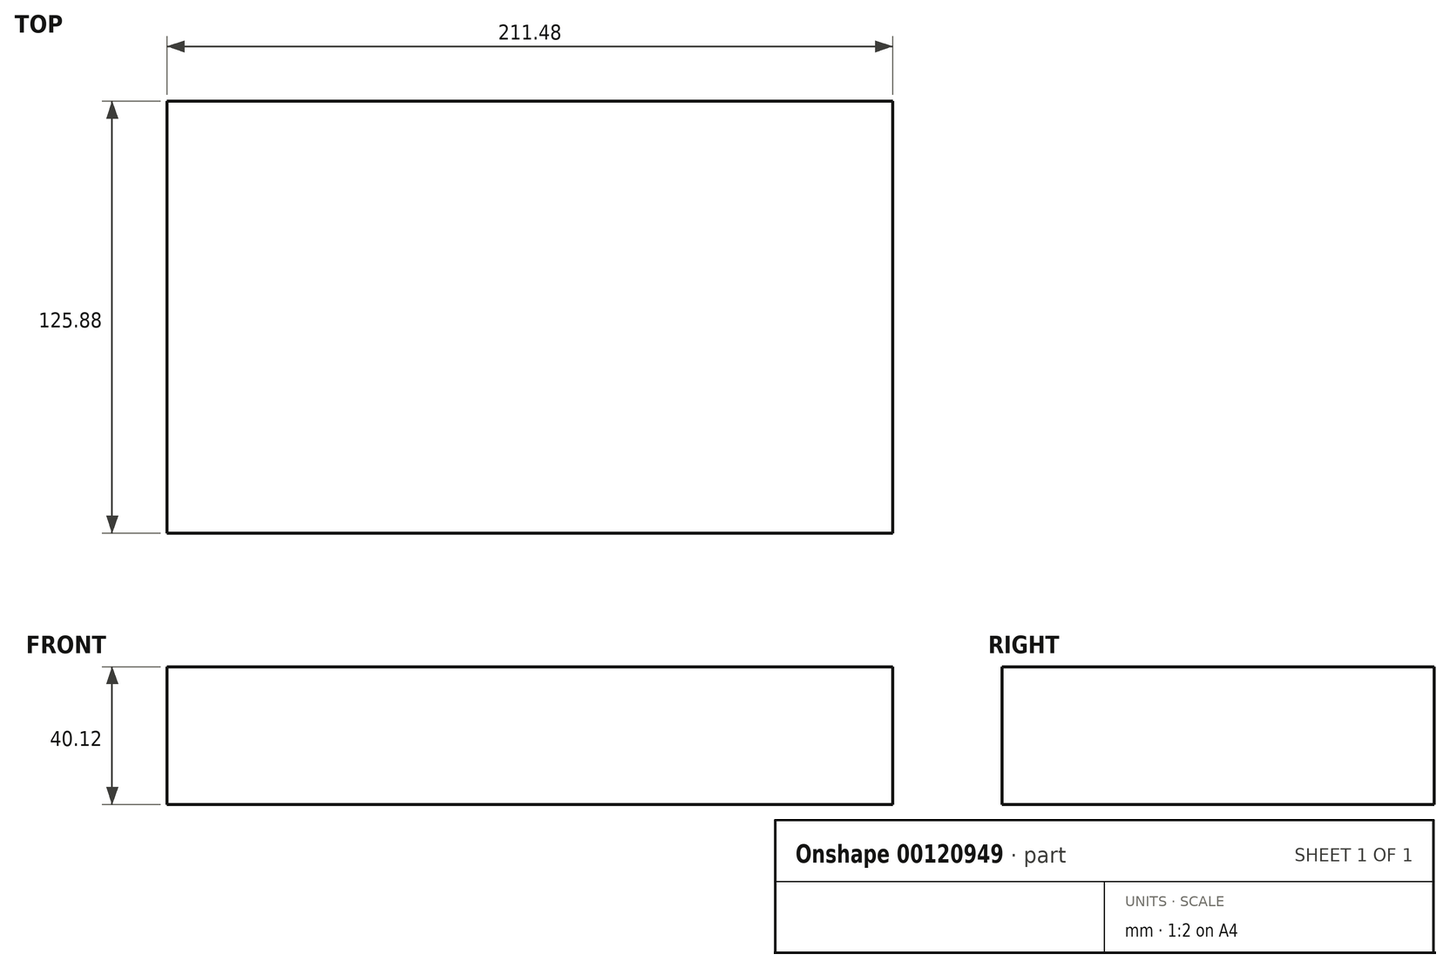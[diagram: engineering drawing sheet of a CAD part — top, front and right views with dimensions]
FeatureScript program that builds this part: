
annotation { "Feature Type Name" : "Feature", "Feature Type Description" : "" }
export const myFeature = defineFeature(function(context is Context, id is Id, definition is map)
    precondition{}
    {
        {
            var Q0;
            Q0=qCreatedBy(makeId("Top.planeOp"),FACE);
            var sketch = newSketch(context, id + "F0", { "sketchPlane" : qUnion([Q0])});
            skLineSegment(sketch, "E0.bottom", {"start": v(-96.13, 62.85) * mm, "end": v(115.35, 62.85) * mm});
            skLineSegment(sketch, "E0.top", {"start": v(-96.13, -63.03) * mm, "end": v(115.35, -63.03) * mm});
            skLineSegment(sketch, "E0.left", {"start": v(-96.13, 62.85) * mm, "end": v(-96.13, -63.03) * mm});
            skLineSegment(sketch, "E0.right", {"start": v(115.35, 62.85) * mm, "end": v(115.35, -63.03) * mm});
            skSolve(sketch);
        }
        {
            var Q0;
            Q0=qCreatedBy(makeId("Top.planeOp"),FACE);
            var sketch = newSketch(context, id + "F1", { "sketchPlane" : qUnion([Q0])});
            skLineSegment(sketch, "E1", {"start": v(-4.14, 45.72) * mm, "end": v(0, 45.72) * mm});
            skLineSegment(sketch, "E2", {"start": v(0, 45.72) * mm, "end": v(0, 38.86) * mm});
            skLineSegment(sketch, "E3", {"start": v(0, 38.86) * mm, "end": v(66.04, 38.86) * mm});
            skLineSegment(sketch, "E4", {"start": v(66.04, 38.86) * mm, "end": v(66.04, -38.86) * mm});
            skLineSegment(sketch, "E5", {"start": v(66.04, -38.86) * mm, "end": v(0, -38.86) * mm});
            skLineSegment(sketch, "E6", {"start": v(0, -38.86) * mm, "end": v(0, -45.72) * mm});
            skLineSegment(sketch, "E7", {"start": v(0, -45.72) * mm, "end": v(-4.14, -45.72) * mm});
            skLineSegment(sketch, "E8", {"start": v(-4.14, -45.72) * mm, "end": v(-4.14, 45.72) * mm});
            skSolve(sketch);
        }
        {
            var Q0;
            Q0=qCreatedBy(makeId("Top.planeOp"),FACE);
            var sketch = newSketch(context, id + "F2", { "sketchPlane" : qUnion([Q0])});
            skLineSegment(sketch, "E9", {"start": v(-4.14, -45.72) * mm, "end": v(-21.09, -45.72) * mm});
            skLineSegment(sketch, "E10", {"start": v(-21.09, -55.88) * mm, "end": v(-21.09, -45.72) * mm});
            skLineSegment(sketch, "E11", {"start": v(-21.09, -55.88) * mm, "end": v(-46.49, -55.88) * mm});
            skLineSegment(sketch, "E12", {"start": v(-46.49, -45.72) * mm, "end": v(-46.49, -55.88) * mm});
            skLineSegment(sketch, "E13", {"start": v(-46.49, -45.72) * mm, "end": v(-66.04, -45.72) * mm});
            skLineSegment(sketch, "E14", {"start": v(-66.04, 45.72) * mm, "end": v(-66.04, -45.72) * mm});
            skLineSegment(sketch, "E15", {"start": v(-66.04, 45.72) * mm, "end": v(-46.48, 45.72) * mm});
            skLineSegment(sketch, "E16", {"start": v(-46.48, 55.88) * mm, "end": v(-46.48, 45.72) * mm});
            skLineSegment(sketch, "E17", {"start": v(-46.48, 55.88) * mm, "end": v(-21.08, 55.88) * mm});
            skLineSegment(sketch, "E18", {"start": v(-21.08, 45.72) * mm, "end": v(-21.08, 55.88) * mm});
            skLineSegment(sketch, "E19", {"start": v(-21.08, 45.72) * mm, "end": v(-4.14, 45.72) * mm});
            skLineSegment(sketch, "E20", {"start": v(-4.14, -45.72) * mm, "end": v(-4.14, 45.72) * mm});
            skSolve(sketch);
        }
        {
            var Q0;
            Q0 = qSketchRegion(id + "F1", true);
            extrude(context, id + "F3", {"entities" : qUnion([Q0]), "depth" : 20.32 * mm});
        }
        {
            var Q0;
            Q0 = qSketchRegion(id + "F2", true);
            extrude(context, id + "F4", {"entities" : qUnion([Q0]), "operationType" : NewBodyOperationType.ADD, "depth" : 30.48 * mm});
        }
        {
            var Q0;
            Q0 = qSketchRegion(id + "F0", true);
            extrude(context, id + "F5", {"entities" : qUnion([Q0]), "operationType" : NewBodyOperationType.ADD, "depth" : 40.12 * mm});
        }
    });
